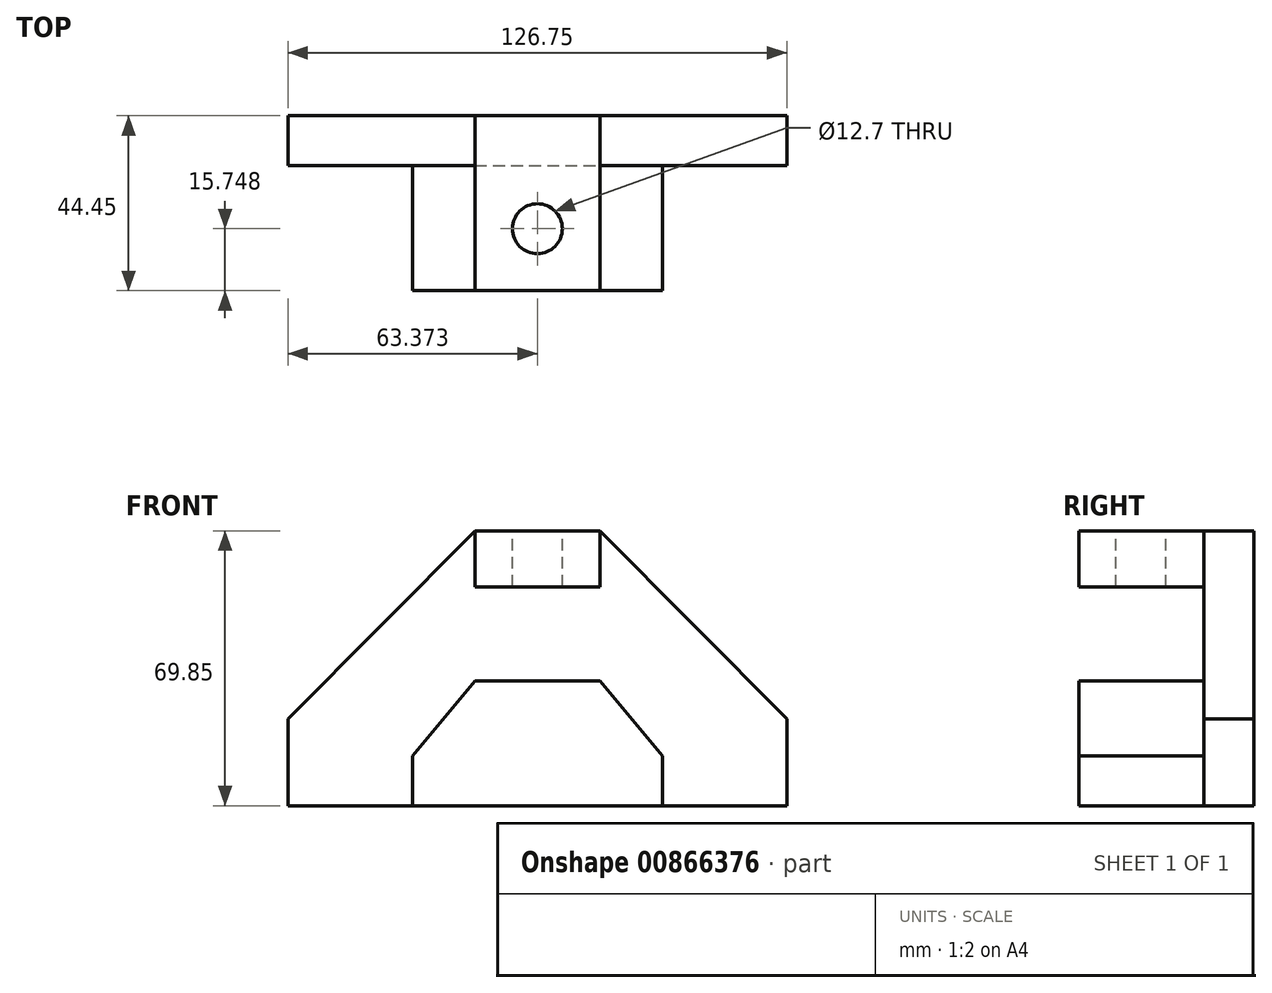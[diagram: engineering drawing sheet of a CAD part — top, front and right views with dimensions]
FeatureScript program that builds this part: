
annotation { "Feature Type Name" : "Feature", "Feature Type Description" : "" }
export const myFeature = defineFeature(function(context is Context, id is Id, definition is map)
    precondition{}
    {
        {
            var Q0;
            Q0=qCreatedBy(makeId("Front.planeOp"),FACE);
            var sketch = newSketch(context, id + "F0", { "sketchPlane" : qUnion([Q0])});
            skLineSegment(sketch, "E0", {"start": v(-32.06, -32.74) * mm, "end": v(-32.06, -10.64) * mm});
            skLineSegment(sketch, "E1", {"start": v(-32.06, -10.64) * mm, "end": v(15.44, 37.1) * mm});
            skLineSegment(sketch, "E2", {"start": v(15.44, 37.1) * mm, "end": v(47.19, 37.1) * mm});
            skLineSegment(sketch, "E3", {"start": v(47.19, 37.1) * mm, "end": v(94.69, -10.64) * mm});
            skLineSegment(sketch, "E4", {"start": v(94.69, -10.64) * mm, "end": v(94.69, -32.74) * mm});
            skLineSegment(sketch, "E5", {"start": v(-32.06, -32.74) * mm, "end": v(94.69, -32.74) * mm});
            skSolve(sketch);
        }
        {
            var Q0;
            Q0=makeQuery(id+"F0.imprint","IMPRINT",FACE,{"disambiguationData":[TD([[makeQuery(id+"F0.imprint","IMPRINT",EDGE,{"derivedFrom":sQuery(id+"F0.wireOp",EDGE,"E0")}),-1.0]])]});
            extrude(context, id + "F1", {"entities" : qUnion([Q0]), "depth" : 12.7 * mm, "offsetDistance" : 25.4 * mm});
        }
        {
            var Q0;
            Q0=makeQuery(id+"F1.opExtrude","CAP_FACE",FACE,{"disambiguationData":[OSD([sQuery(id+"F0.wireOp",EDGE,"E0"),sQuery(id+"F0.wireOp",EDGE,"E1"),sQuery(id+"F0.wireOp",EDGE,"E2"),sQuery(id+"F0.wireOp",EDGE,"E3"),sQuery(id+"F0.wireOp",EDGE,"E4"),sQuery(id+"F0.wireOp",EDGE,"E5")])],"isStart":false});
            var sketch = newSketch(context, id + "F2", { "sketchPlane" : qUnion([Q0])});
            skLineSegment(sketch, "E6", {"start": v(15.44, 37.1) * mm, "end": v(15.44, 22.88) * mm});
            skLineSegment(sketch, "E7", {"start": v(15.44, 22.88) * mm, "end": v(47.19, 22.88) * mm});
            skLineSegment(sketch, "E8", {"start": v(47.19, 37.1) * mm, "end": v(47.19, 22.88) * mm});
            skLineSegment(sketch, "E9", {"start": v(15.44, -1) * mm, "end": v(47.19, -1) * mm});
            skLineSegment(sketch, "E10", {"start": v(47.19, -1) * mm, "end": v(63.06, -20.04) * mm});
            skLineSegment(sketch, "E11", {"start": v(63.06, -20.04) * mm, "end": v(63.06, -32.74) * mm});
            skLineSegment(sketch, "E12", {"start": v(15.44, -1) * mm, "end": v(-0.44, -20.04) * mm});
            skLineSegment(sketch, "E13", {"start": v(-0.44, -20.04) * mm, "end": v(-0.44, -32.74) * mm});
            skSolve(sketch);
        }
        {
            var Q0;
            Q0=makeQuery(id+"F2.imprint","IMPRINT",FACE,{"disambiguationData":[TD([[makeQuery(id+"F2.imprint","IMPRINT",EDGE,{"derivedFrom":sQuery(id+"F2.wireOp",EDGE,"E6")}),1.0]])]});
            var Q1;
            Q1=makeQuery(id+"F2.imprint","IMPRINT",FACE,{"disambiguationData":[TD([[makeQuery(id+"F2.imprint","IMPRINT",EDGE,{"derivedFrom":sQuery(id+"F2.wireOp",EDGE,"E9")}),-1.0]])]});
            extrude(context, id + "F3", {"entities" : qUnion([Q0, Q1]), "operationType" : NewBodyOperationType.ADD, "depth" : 31.75 * mm, "offsetDistance" : 25.4 * mm});
        }
        {
            var Q0;
            {var subQ0=sQuery(id+"F0.wireOp",EDGE,"E2");Q0=makeQuery(id+"F3.boolean.opBoolean","MERGE",FACE,{"derivedFrom":[makeQuery(id+"F1.opExtrude","SWEPT_FACE",FACE,{"disambiguationData":[OSD([subQ0])]}),makeQuery(id+"F3.opExtrude","SWEPT_FACE",FACE,{"disambiguationData":[OSD([subQ0])]})]});}
            var sketch = newSketch(context, id + "F4", { "sketchPlane" : qUnion([Q0])});
            skCircle(sketch, "E14", {"center": v(31.31, -28.7) * mm, "radius": 6.35 * mm});
            skPoint(sketch, "E14.centerSnap0", {"position": v(31.31, -44.45) * mm});
            skSolve(sketch);
        }
        {
            var Q0;
            Q0=makeQuery(id+"F4.imprint","IMPRINT",FACE,{"disambiguationData":[TD([[makeQuery(id+"F4.imprint","IMPRINT",EDGE,{"derivedFrom":sQuery(id+"F4.wireOp",EDGE,"E14")}),1.0]])]});
            extrude(context, id + "F5", {"entities" : qUnion([Q0]), "operationType" : NewBodyOperationType.REMOVE, "oppositeDirection" : true, "depth" : 25.4 * mm, "offsetDistance" : 25.4 * mm});
        }
    });
